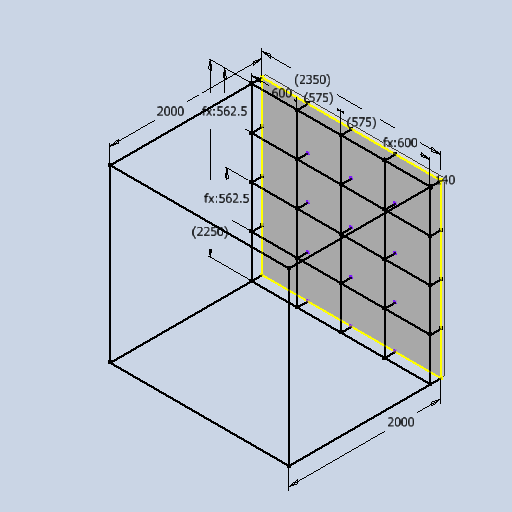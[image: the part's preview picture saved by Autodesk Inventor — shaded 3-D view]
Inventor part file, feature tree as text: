
AUTODESK INVENTOR PART (.ipt)
format: ipt  version: 2024.2 (Build 282272000, 272)  size: 127,488 bytes
history: native  units: mm
features: extrude x1, sketch x1
ambient origin geometry x8: Origin, YZ Plane, XZ Plane, XY Plane, X Axis, Y Axis, Z Axis, Center Point
bodies: Solid1 (feature_tree)
feature tree (2):
  extrude  "Extrusion1"  Depth=2350.0mm
  sketch  "3D Sketch1"
